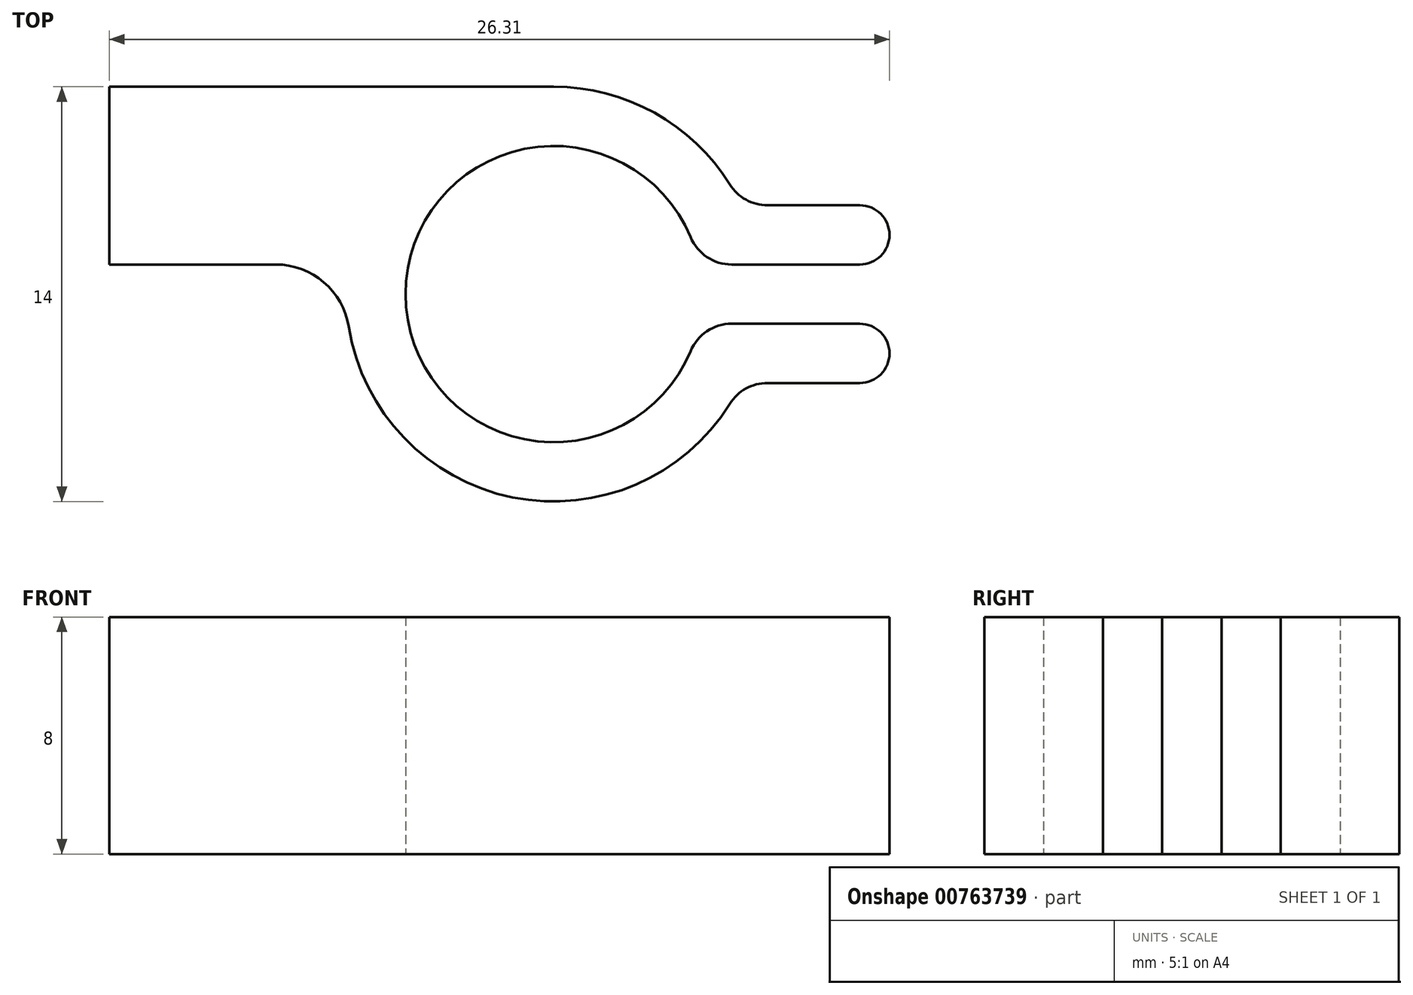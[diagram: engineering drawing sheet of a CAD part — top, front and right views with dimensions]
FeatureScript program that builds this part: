
annotation { "Feature Type Name" : "Feature", "Feature Type Description" : "" }
export const myFeature = defineFeature(function(context is Context, id is Id, definition is map)
    precondition{}
    {
        {
            var Q0;
            Q0=qCreatedBy(makeId("Top.planeOp"),FACE);
            var sketch = newSketch(context, id + "F0", { "sketchPlane" : qUnion([Q0])});
            skLineSegment(sketch, "E0.bottom", {"start": v(0, 0) * mm, "end": v(8, 0) * mm});
            skLineSegment(sketch, "E0.top", {"start": v(0, -6) * mm, "end": v(5.6, -6) * mm});
            skLineSegment(sketch, "E0.left", {"start": v(0, 0) * mm, "end": v(0, -6) * mm});
            skLineSegment(sketch, "E1", {"start": v(-1.2, -3) * mm, "end": v(18.45, -3) * mm, "construction": true});
            skPoint(sketch, "E1.startSnap0", {"position": v(0, -3) * mm});
            skLineSegment(sketch, "E2", {"start": v(7.97, 1.86) * mm, "end": v(7.97, 0) * mm, "construction": true});
            skLineSegment(sketch, "E3", {"start": v(8, 0) * mm, "end": v(14.99, 0) * mm});
            skArc(sketch, "E4", {"start": v(8.08, -8.1) * mm, "mid": v(13.6, -13.86) * mm, "end": v(20.93, -10.7) * mm});
            skArc(sketch, "E5", {"start": v(19.6, -5.08) * mm, "mid": v(9.99, -7) * mm, "end": v(19.6, -8.92) * mm});
            skLineSegment(sketch, "E6", {"start": v(6.58, -7) * mm, "end": v(24.77, -7) * mm, "construction": true});
            skLineSegment(sketch, "E7.bottom", {"start": v(22.2, -4) * mm, "end": v(25.31, -4) * mm});
            skLineSegment(sketch, "E7.top", {"start": v(21.92, -6) * mm, "end": v(25.31, -6) * mm});
            skLineSegment(sketch, "E7.right", {"start": v(26.31, -5) * mm, "end": v(26.31, -5) * mm});
            skLineSegment(sketch, "E8.MirrorCS", {"start": v(21.92, -8) * mm, "end": v(25.31, -8) * mm});
            skLineSegment(sketch, "E9.MirrorCS", {"start": v(26.31, -9) * mm, "end": v(26.31, -9) * mm});
            skLineSegment(sketch, "E10.MirrorCS", {"start": v(22.2, -10) * mm, "end": v(25.31, -10) * mm});
            skLineSegment(sketch, "E11.trimOffspring", {"start": v(7.99, -7) * mm, "end": v(8, -12.1) * mm, "construction": true});
            skPoint(sketch, "E12.orphan", {"position": v(21.31, -6) * mm});
            skArc(sketch, "E13.trimOffspring", {"start": v(20.93, -3.3) * mm, "mid": v(18.38, -0.88) * mm, "end": v(14.99, 0) * mm});
            skPoint(sketch, "E14.orphan", {"position": v(21.31, -8) * mm});
            skLineSegment(sketch, "E15", {"start": v(21.92, -6) * mm, "end": v(20.99, -6) * mm});
            skLineSegment(sketch, "E16", {"start": v(21.92, -8) * mm, "end": v(20.99, -8) * mm});
            skPoint(sketch, "E17.visualSharp", {"position": v(21.31, -4) * mm});
            skArc(sketch, "E17.filletArc", {"start": v(20.93, -3.3) * mm, "mid": v(21.47, -3.81) * mm, "end": v(22.2, -4) * mm});
            skPoint(sketch, "E18.visualSharp", {"position": v(21.31, -10) * mm});
            skArc(sketch, "E18.filletArc", {"start": v(22.2, -10) * mm, "mid": v(21.47, -10.19) * mm, "end": v(20.93, -10.7) * mm});
            skPoint(sketch, "E19.visualSharp", {"position": v(19.89, -6) * mm});
            skArc(sketch, "E19.filletArc", {"start": v(19.6, -5.08) * mm, "mid": v(20.16, -5.75) * mm, "end": v(20.99, -6) * mm});
            skPoint(sketch, "E20.visualSharp", {"position": v(19.89, -8) * mm});
            skArc(sketch, "E20.filletArc", {"start": v(20.99, -8) * mm, "mid": v(20.16, -8.25) * mm, "end": v(19.6, -8.92) * mm});
            skPoint(sketch, "E21.newPointA", {"position": v(8, -6) * mm});
            skArc(sketch, "E21.filletArc", {"start": v(8.08, -8.1) * mm, "mid": v(7.23, -6.6) * mm, "end": v(5.6, -6) * mm});
            skPoint(sketch, "E22.visualSharp", {"position": v(26.31, -6) * mm});
            skArc(sketch, "E22.filletArc", {"start": v(25.31, -6) * mm, "mid": v(26.02, -5.7) * mm, "end": v(26.31, -5) * mm});
            skPoint(sketch, "E23.visualSharp", {"position": v(26.31, -4) * mm});
            skArc(sketch, "E23.filletArc", {"start": v(26.31, -5) * mm, "mid": v(26.02, -4.3) * mm, "end": v(25.31, -4) * mm});
            skPoint(sketch, "E24.visualSharp", {"position": v(26.31, -8) * mm});
            skArc(sketch, "E24.filletArc", {"start": v(26.31, -9) * mm, "mid": v(26.02, -8.3) * mm, "end": v(25.31, -8) * mm});
            skPoint(sketch, "E25.visualSharp", {"position": v(26.31, -10) * mm});
            skArc(sketch, "E25.filletArc", {"start": v(25.31, -10) * mm, "mid": v(26.02, -9.7) * mm, "end": v(26.31, -9) * mm});
            skSolve(sketch);
        }
        {
            var Q0;
            Q0=makeQuery(id+"F0.imprint","IMPRINT",FACE,{"disambiguationData":[TD([[makeQuery(id+"F0.imprint","IMPRINT",EDGE,{"derivedFrom":sQuery(id+"F0.wireOp",EDGE,"E0.bottom")}),-1.0]])]});
            extrude(context, id + "F1", {"entities" : qUnion([Q0]), "depth" : 8 * mm, "offsetDistance" : 25 * mm});
        }
    });
